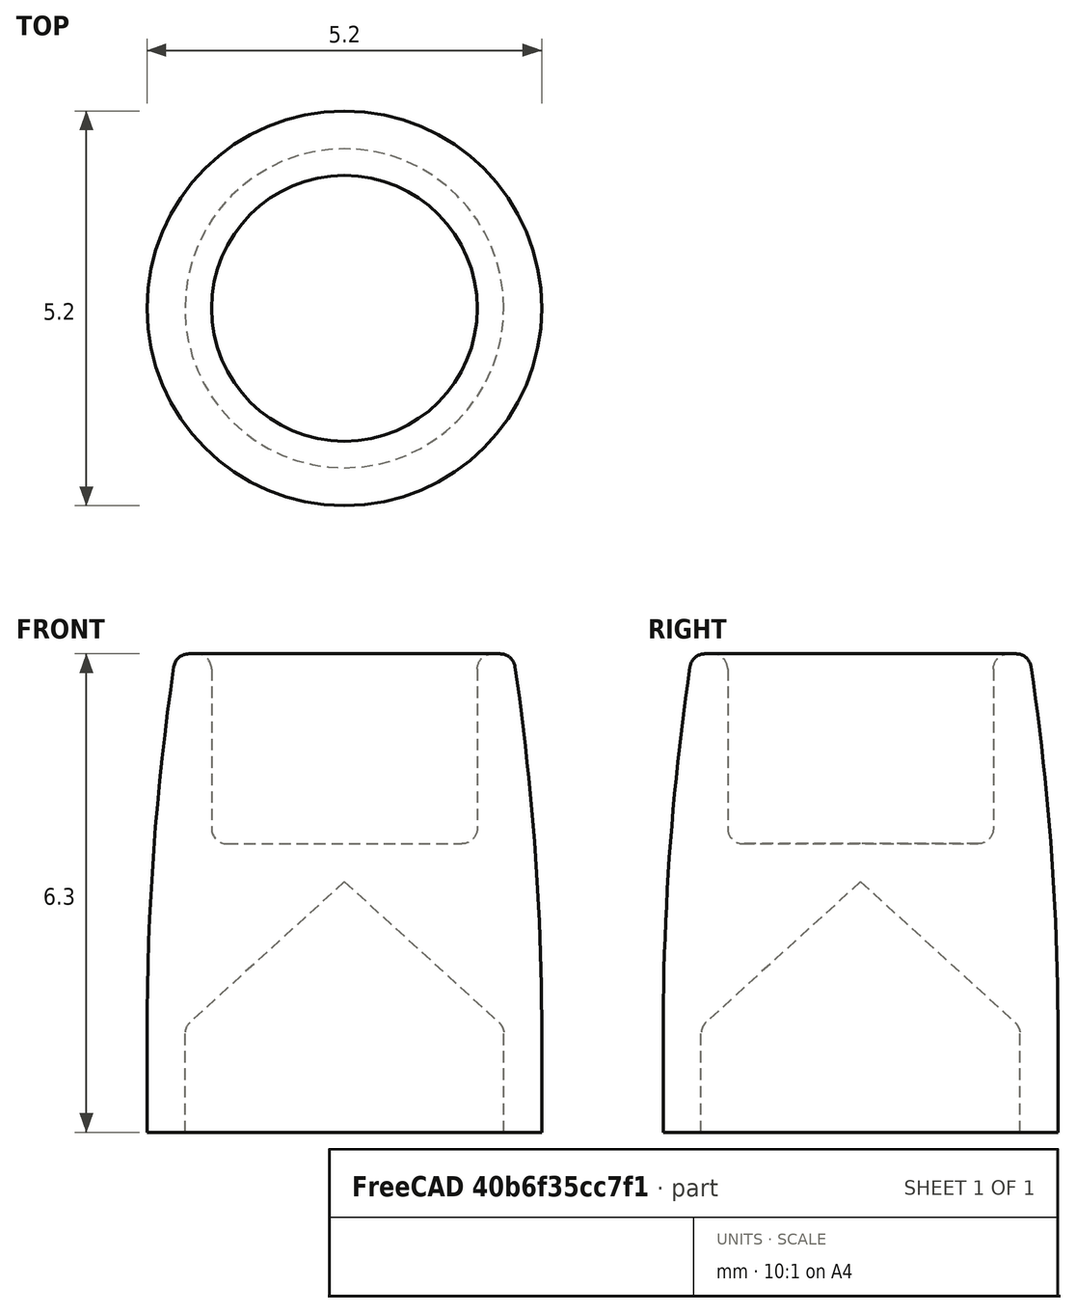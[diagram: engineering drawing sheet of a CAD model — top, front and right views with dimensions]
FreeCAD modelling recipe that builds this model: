
FCSTD DOCUMENT  (FreeCAD 0.18R16093 +53 (Git))
Label: MagnetHolderD3.5L5
License: All rights reserved
LicenseURL: http://en.wikipedia.org/wiki/All_rights_reserved
objects: Sketcher::SketchObject×1, PartDesign::Revolution×1, PartDesign::Body×1
note: 4 computed .brp shape members not serialized (recipe doc carries the construction recipe); baked Part::Feature solids carry a one-line shape summary decoded from their .brp

FEATURE [Sketcher::SketchObject] Sketch
  MapMode = 5
  Placement = pos=(0,0,0) rot=(1,0,0;1.5708rad)
  Support = -> [XZ_Plane]
  sketch-geometry (13):
    g0: LineSegment StartX=-2.6 StartY=0 StartZ=0 EndX=-2.6 EndY=-1.3 EndZ=0
    g1: LineSegment StartX=-2.6 StartY=-1.3 StartZ=0 EndX=-2.1 EndY=-1.3 EndZ=0
    g2: LineSegment StartX=-2.1 StartY=-1.3 StartZ=0 EndX=-2.1 EndY=0 EndZ=0
    g3: ArcOfCircle CenterX=30.6893 CenterY=0 CenterZ=0 NormalX=0 NormalY=0 NormalZ=1 AngleXU=0 Radius=33.2893 StartAngle=2.99602 EndAngle=3.14159
    g4: LineSegment StartX=-1.75 StartY=4.8 StartZ=0 EndX=-1.75 EndY=2.7 EndZ=0
    g5: LineSegment StartX=0 StartY=2.5 StartZ=0 EndX=0 EndY=2 EndZ=0
    g6: ArcOfCircle CenterX=-2.05 CenterY=4.8 CenterZ=0 NormalX=0 NormalY=0 NormalZ=1 AngleXU=0 Radius=0.2 StartAngle=1.5708 EndAngle=2.99602
    g7: LineSegment StartX=-2.05 StartY=5 StartZ=0 EndX=-1.95 EndY=5 EndZ=0
    g8: ArcOfCircle CenterX=-1.95 CenterY=4.8 CenterZ=0 NormalX=0 NormalY=0 NormalZ=1 AngleXU=0 Radius=0.2 StartAngle=-9e-16 EndAngle=1.5708
    g9: ArcOfCircle CenterX=-1.55 CenterY=2.7 CenterZ=0 NormalX=0 NormalY=0 NormalZ=1 AngleXU=0 Radius=0.2 StartAngle=3.14159 EndAngle=4.71239
    g10: LineSegment StartX=-1.55 StartY=2.5 StartZ=0 EndX=0 EndY=2.5 EndZ=0
    g11: LineSegment StartX=0 StartY=2 StartZ=0 EndX=-2.03463 EndY=0.1479 EndZ=0
    g12: ArcOfCircle CenterX=-1.9 CenterY=0 CenterZ=0 NormalX=0 NormalY=0 NormalZ=1 AngleXU=0 Radius=0.2 StartAngle=2.30927 EndAngle=3.14159
  constraints (35):
    c: Vertical(g0)
    c: Vertical(g2)
    c: Coincident(g1,g0)
    c: Coincident(g2,g1)
    c: Horizontal(g1)
    c: PointOnObject(g2,g-1)
    c: Tangent(g3,g0) = -1.5708
    c: DistanceX(g1,g1) = 0.5
    c: DistanceX(g2) = -2.1
    c: DistanceY(g2,g2) = 1.3
    c: PointOnObject(g5,g-2)
    c: Vertical(g4)
    c: Vertical(g5)
    c: Radius(g6) = 0.2
    c: Horizontal(g7)
    c: Tangent(g6,g7) = 1.5708
    c: Tangent(g8,g7) = 1.5708
    c: DistanceY(g7) = 5
    c: Tangent(g4,g8) = 1.5708
    c: DistanceX(g4) = -1.75
    c: Equal(g6,g8)
    c: Horizontal(g10)
    c: Tangent(g9,g4) = -1.5708
    c: Tangent(g9,g10) = -1.5708
    c: Coincident(g10,g5)
    c: Equal(g8,g9)
    c: DistanceY(g5,g5) = 0.5
    c: DistanceY(g9,g7) = 2.5
    c: Tangent(g3,g6) = -1.5708
    c: DistanceX(g7,g7) = 0.1
    c: PointOnObject(g0,g-1)
    c: Coincident(g11,g5)
    c: Tangent(g12,g11) = -1.5708
    c: Tangent(g12,g2) = 1.5708
    c: Equal(g12,g9)
FEATURE [PartDesign::Revolution] Revolution
  Angle = 360
  Axis = (0,2e-16,1)
  Base = (0,0,0)
  Placement = pos=(0,0,0) rot=(1,0,0;1.5708rad)
  Profile = -> Sketch
  ReferenceAxis = -> Sketch [V_Axis]
FEATURE [PartDesign::Body] Body
  Group = -> [Sketch,Revolution]
  Origin = -> Origin
  Tip = -> Revolution
